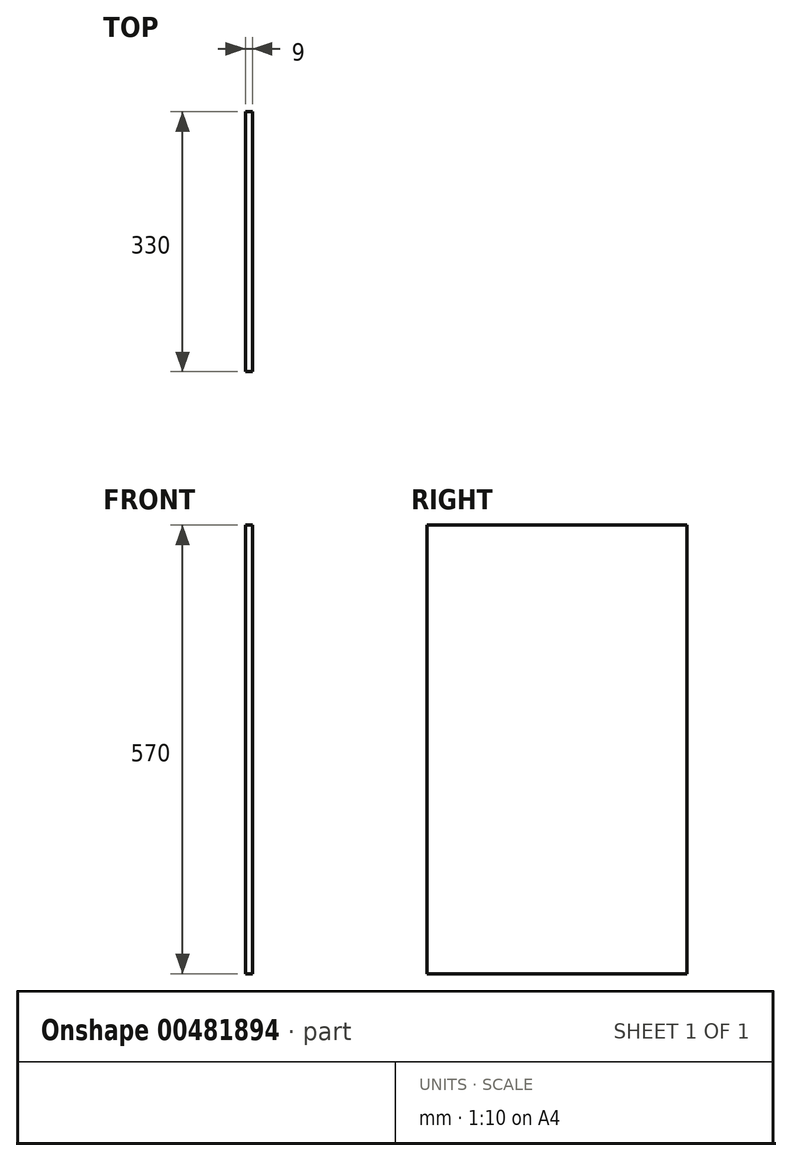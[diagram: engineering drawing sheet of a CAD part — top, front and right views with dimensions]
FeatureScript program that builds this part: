
annotation { "Feature Type Name" : "Feature", "Feature Type Description" : "" }
export const myFeature = defineFeature(function(context is Context, id is Id, definition is map)
    precondition{}
    {
        {
            var Q0;
            Q0=qCreatedBy(makeId("Right.planeOp"),FACE);
            var sketch = newSketch(context, id + "F0", { "sketchPlane" : qUnion([Q0])});
            skLineSegment(sketch, "E0.bottom", {"start": v(0, 0) * mm, "end": v(330, 0) * mm});
            skLineSegment(sketch, "E0.top", {"start": v(0, 570) * mm, "end": v(330, 570) * mm});
            skLineSegment(sketch, "E0.left", {"start": v(0, 0) * mm, "end": v(0, 570) * mm});
            skLineSegment(sketch, "E1", {"start": v(330, 570) * mm, "end": v(330, 0) * mm});
            skSolve(sketch);
        }
        {
            var Q0;
            Q0 = qSketchRegion(id + "F0", true);
            extrude(context, id + "F1", {"entities" : qUnion([Q0]), "depth" : 9 * mm});
        }
    });
